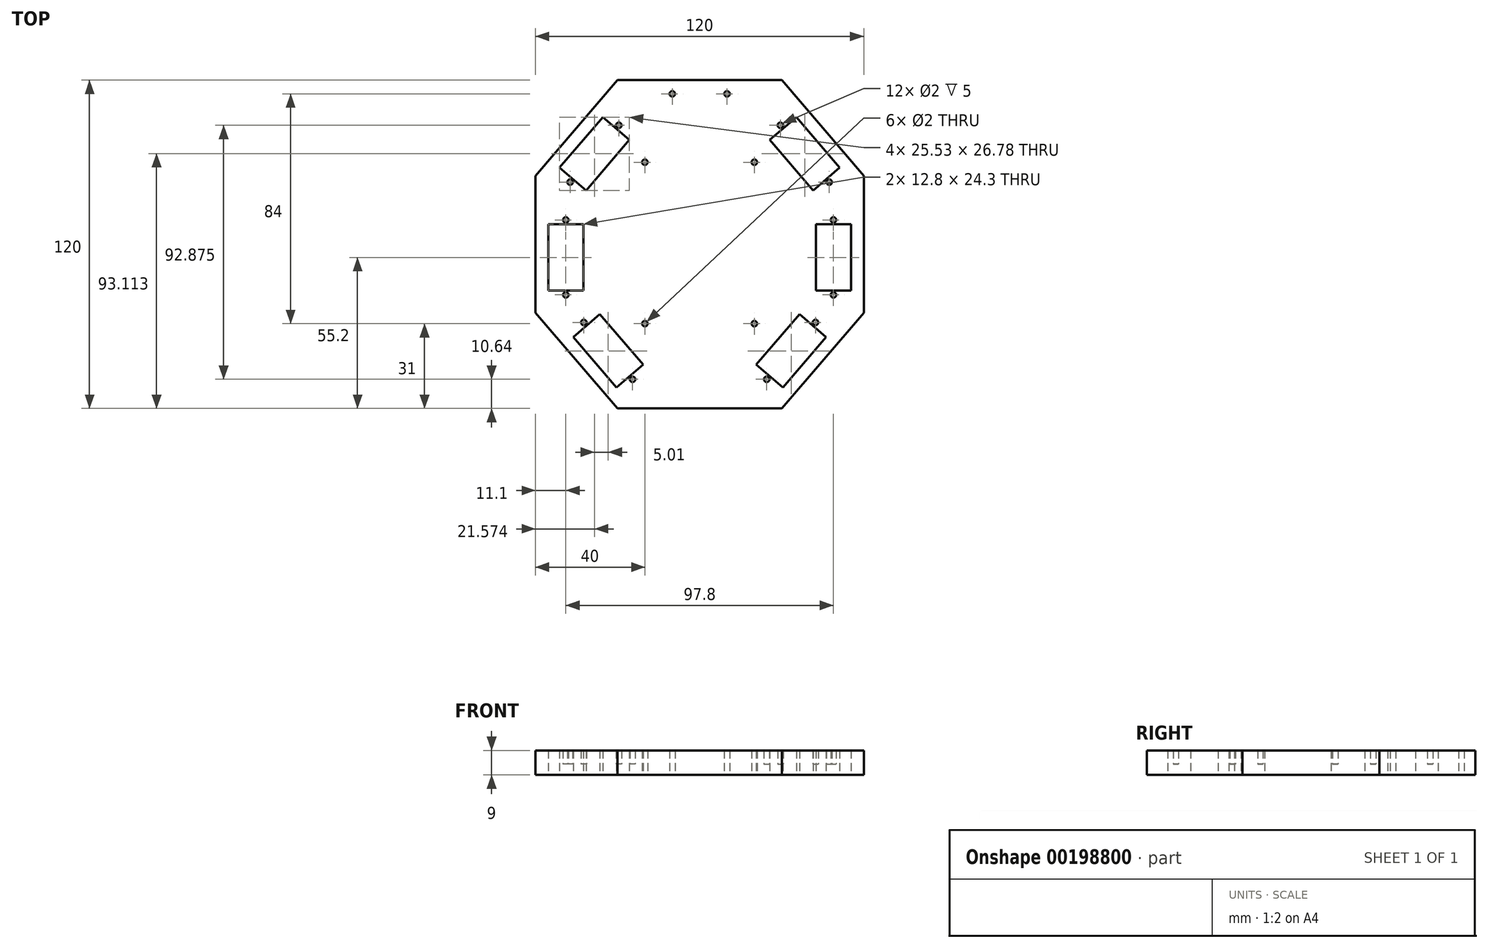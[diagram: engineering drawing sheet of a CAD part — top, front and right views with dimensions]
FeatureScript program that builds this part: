
annotation { "Feature Type Name" : "Feature", "Feature Type Description" : "" }
export const myFeature = defineFeature(function(context is Context, id is Id, definition is map)
    precondition{}
    {
        {
            var Q0;
            Q0=qCreatedBy(makeId("Top.planeOp"),FACE);
            var sketch = newSketch(context, id + "F0", { "sketchPlane" : qUnion([Q0])});
            skLineSegment(sketch, "E0.left", {"start": v(-40, -25) * mm, "end": v(-40, 25) * mm});
            skPoint(sketch, "E0.middle", {"position": v(0, 0) * mm});
            skLineSegment(sketch, "E1", {"start": v(-40, 25) * mm, "end": v(-10, 60) * mm});
            skLineSegment(sketch, "E2", {"start": v(-10, -60) * mm, "end": v(-40, -25) * mm});
            skLineSegment(sketch, "E3", {"start": v(-32.39, -33.88) * mm, "end": v(-19.1, -22.5) * mm});
            skLineSegment(sketch, "E4", {"start": v(-19.1, -22.5) * mm, "end": v(1.99, -47.1) * mm});
            skLineSegment(sketch, "E5", {"start": v(1.99, -47.1) * mm, "end": v(-11.3, -58.48) * mm});
            skLineSegment(sketch, "E6", {"start": v(-28.82, -30.82) * mm, "end": v(-7.73, -55.42) * mm});
            skLineSegment(sketch, "E7", {"start": v(-10, 60) * mm, "end": v(20, 60) * mm});
            skLineSegment(sketch, "E8", {"start": v(20, -60) * mm, "end": v(-10, -60) * mm});
            skLineSegment(sketch, "E9", {"start": v(20, -60) * mm, "end": v(20, 60) * mm});
            skLineSegment(sketch, "E10", {"start": v(-40, -21) * mm, "end": v(-22.5, -21) * mm});
            skLineSegment(sketch, "E11", {"start": v(-22.5, -21) * mm, "end": v(-22.5, 11.4) * mm});
            skLineSegment(sketch, "E12", {"start": v(-22.5, 11.4) * mm, "end": v(-40, 11.4) * mm});
            skLineSegment(sketch, "E13", {"start": v(-35.3, 11.4) * mm, "end": v(-35.3, -21) * mm});
            skLineSegment(sketch, "E14", {"start": v(-16.31, 52.64) * mm, "end": v(-3.02, 41.25) * mm});
            skLineSegment(sketch, "E15", {"start": v(-3.02, 41.25) * mm, "end": v(-24.1, 16.65) * mm});
            skLineSegment(sketch, "E16", {"start": v(-24.1, 16.65) * mm, "end": v(-37.4, 28.04) * mm});
            skLineSegment(sketch, "E17", {"start": v(-12.74, 49.58) * mm, "end": v(-33.83, 24.98) * mm});
            skLineSegment(sketch, "E18", {"start": v(-16.46, -25.57) * mm, "end": v(-26.18, -33.9) * mm});
            skLineSegment(sketch, "E19", {"start": v(-0.65, -44.02) * mm, "end": v(-10.37, -52.35) * mm});
            skLineSegment(sketch, "E20", {"start": v(-22.5, -16.95) * mm, "end": v(-35.3, -16.95) * mm});
            skLineSegment(sketch, "E21", {"start": v(-22.5, 7.35) * mm, "end": v(-35.3, 7.35) * mm});
            skLineSegment(sketch, "E22", {"start": v(-21.47, 19.72) * mm, "end": v(-31.2, 28.05) * mm});
            skLineSegment(sketch, "E23", {"start": v(-5.66, 38.17) * mm, "end": v(-15.38, 46.5) * mm});
            skCircle(sketch, "E24", {"center": v(-9.51, 43.52) * mm, "radius": 1 * mm});
            skCircle(sketch, "E25", {"center": v(-27.34, 22.71) * mm, "radius": 1 * mm});
            skCircle(sketch, "E26", {"center": v(-28.9, 8.9) * mm, "radius": 1 * mm});
            skCircle(sketch, "E27", {"center": v(-28.9, -18.5) * mm, "radius": 1 * mm});
            skCircle(sketch, "E28", {"center": v(-22.33, -28.56) * mm, "radius": 1 * mm});
            skCircle(sketch, "E29", {"center": v(-4.5, -49.36) * mm, "radius": 1 * mm});
            skCircle(sketch, "E30", {"center": v(10, 55) * mm, "radius": 1 * mm});
            skCircle(sketch, "E31", {"center": v(0, 30) * mm, "radius": 1 * mm});
            skCircle(sketch, "E32", {"center": v(0, -29) * mm, "radius": 1 * mm});
            skSolve(sketch);
        }
        {
            var Q0;
            Q0 = qSketchRegion(id + "F0", true);
            var Q1;
            {var subQ3=sQuery(id+"F0.wireOp",EDGE,"E19");Q1=makeQuery(id+"F0.imprint","IMPRINT",FACE,{"disambiguationData":[TD([[makeQuery(id+"F0.imprint","IMPRINT",EDGE,{"derivedFrom":subQ3}),1.0]])]});}
            var Q2;
            {var subQ0=sQuery(id+"F0.wireOp",EDGE,"E18");Q2=makeQuery(id+"F0.imprint","IMPRINT",FACE,{"disambiguationData":[TD([[makeQuery(id+"F0.imprint","IMPRINT",EDGE,{"derivedFrom":subQ0}),-1.0]])]});}
            var Q3;
            {var subQ0=sQuery(id+"F0.wireOp",EDGE,"E20");Q3=makeQuery(id+"F0.imprint","IMPRINT",FACE,{"disambiguationData":[TD([[makeQuery(id+"F0.imprint","IMPRINT",EDGE,{"derivedFrom":subQ0}),1.0]])]});}
            var Q4;
            {var subQ0=sQuery(id+"F0.wireOp",EDGE,"E21");Q4=makeQuery(id+"F0.imprint","IMPRINT",FACE,{"disambiguationData":[TD([[makeQuery(id+"F0.imprint","IMPRINT",EDGE,{"derivedFrom":subQ0}),-1.0]])]});}
            var Q5;
            {var subQ0=sQuery(id+"F0.wireOp",EDGE,"E23");Q5=makeQuery(id+"F0.imprint","IMPRINT",FACE,{"disambiguationData":[TD([[makeQuery(id+"F0.imprint","IMPRINT",EDGE,{"derivedFrom":subQ0}),-1.0]])]});}
            var Q6;
            {var subQ0=sQuery(id+"F0.wireOp",EDGE,"E22");Q6=makeQuery(id+"F0.imprint","IMPRINT",FACE,{"disambiguationData":[TD([[makeQuery(id+"F0.imprint","IMPRINT",EDGE,{"derivedFrom":subQ0}),1.0]])]});}
            extrude(context, id + "F1", {"entities" : qUnion([Q0, Q1, Q2, Q3, Q4, Q5, Q6]), "depth" : 9 * mm});
        }
        {
            var Q0;
            Q0=makeQuery(id+"F0.imprint","IMPRINT",FACE,{"disambiguationData":[TD([[makeQuery(id+"F0.imprint","IMPRINT",EDGE,{"derivedFrom":sQuery(id+"F0.wireOp",EDGE,"E24")}),1.0]])]});
            var Q1;
            Q1=makeQuery(id+"F0.imprint","IMPRINT",FACE,{"disambiguationData":[TD([[makeQuery(id+"F0.imprint","IMPRINT",EDGE,{"derivedFrom":sQuery(id+"F0.wireOp",EDGE,"E25")}),1.0]])]});
            var Q2;
            Q2=makeQuery(id+"F0.imprint","IMPRINT",FACE,{"disambiguationData":[TD([[makeQuery(id+"F0.imprint","IMPRINT",EDGE,{"derivedFrom":sQuery(id+"F0.wireOp",EDGE,"E26")}),1.0]])]});
            var Q3;
            Q3=makeQuery(id+"F0.imprint","IMPRINT",FACE,{"disambiguationData":[TD([[makeQuery(id+"F0.imprint","IMPRINT",EDGE,{"derivedFrom":sQuery(id+"F0.wireOp",EDGE,"E27")}),1.0]])]});
            var Q4;
            Q4=makeQuery(id+"F0.imprint","IMPRINT",FACE,{"disambiguationData":[TD([[makeQuery(id+"F0.imprint","IMPRINT",EDGE,{"derivedFrom":sQuery(id+"F0.wireOp",EDGE,"E28")}),1.0]])]});
            var Q5;
            Q5=makeQuery(id+"F0.imprint","IMPRINT",FACE,{"disambiguationData":[TD([[makeQuery(id+"F0.imprint","IMPRINT",EDGE,{"derivedFrom":sQuery(id+"F0.wireOp",EDGE,"E29")}),1.0]])]});
            extrude(context, id + "F2", {"entities" : qUnion([Q0, Q1, Q2, Q3, Q4, Q5]), "operationType" : NewBodyOperationType.ADD, "depth" : 4 * mm});
        }
        {
            var Q0;
            Q0=makeQuery(id+"F1.opExtrude","SWEPT_BODY",BODY,{"disambiguationData":[OSD([sQuery(id+"F0.wireOp",EDGE,"E0.left"),sQuery(id+"F0.wireOp",EDGE,"E1"),sQuery(id+"F0.wireOp",EDGE,"E2"),sQuery(id+"F0.wireOp",EDGE,"E4"),sQuery(id+"F0.wireOp",EDGE,"E6"),sQuery(id+"F0.wireOp",EDGE,"E7"),sQuery(id+"F0.wireOp",EDGE,"E8"),sQuery(id+"F0.wireOp",EDGE,"E9"),sQuery(id+"F0.wireOp",EDGE,"E11"),sQuery(id+"F0.wireOp",EDGE,"E13"),sQuery(id+"F0.wireOp",EDGE,"E15"),sQuery(id+"F0.wireOp",EDGE,"E17"),sQuery(id+"F0.wireOp",EDGE,"E18"),sQuery(id+"F0.wireOp",EDGE,"E19"),sQuery(id+"F0.wireOp",EDGE,"E20"),sQuery(id+"F0.wireOp",EDGE,"E21"),sQuery(id+"F0.wireOp",EDGE,"E22"),sQuery(id+"F0.wireOp",EDGE,"E23"),sQuery(id+"F0.wireOp",EDGE,"E24"),sQuery(id+"F0.wireOp",EDGE,"E25"),sQuery(id+"F0.wireOp",EDGE,"E26"),sQuery(id+"F0.wireOp",EDGE,"E27"),sQuery(id+"F0.wireOp",EDGE,"E28"),sQuery(id+"F0.wireOp",EDGE,"E29"),sQuery(id+"F0.wireOp",EDGE,"E30")])]});
            var Q1;
            Q1=makeQuery(id+"F1.opExtrude","SWEPT_FACE",FACE,{"disambiguationData":[OSD([sQuery(id+"F0.wireOp",EDGE,"E9")])]});
            mirror(context, id + "F3", {"operationType" : NewBodyOperationType.ADD, "entities" : qUnion([Q0]), "mirrorPlane" : qUnion([Q1])});
        }
    });
